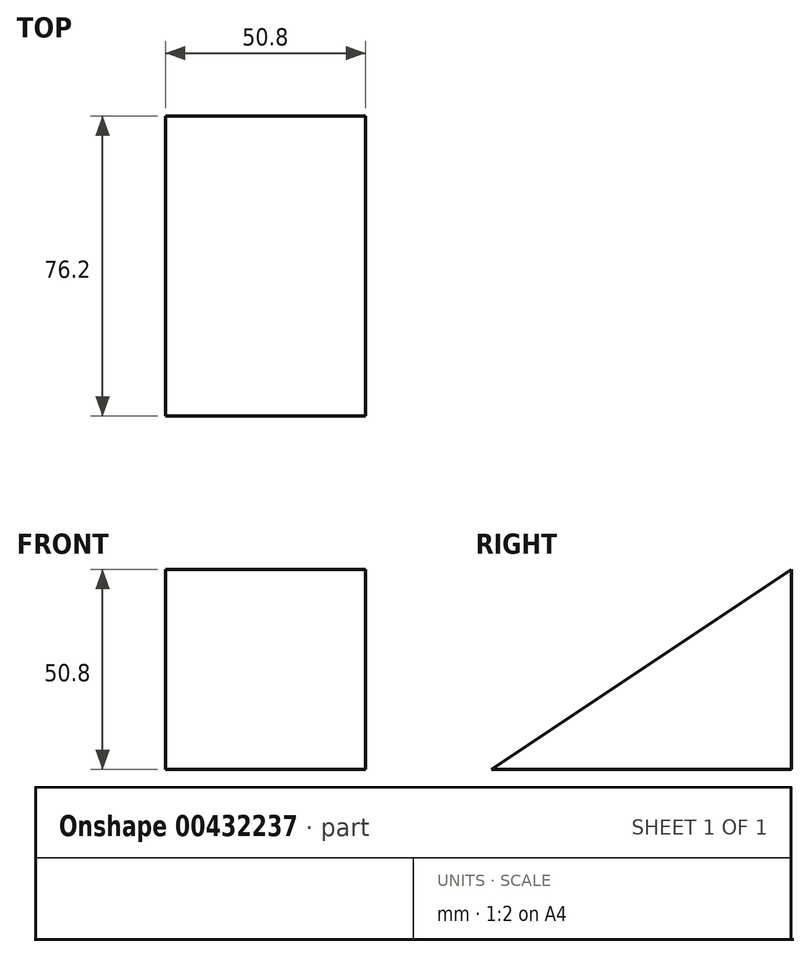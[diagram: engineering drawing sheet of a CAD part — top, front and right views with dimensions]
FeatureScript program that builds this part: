
annotation { "Feature Type Name" : "Feature", "Feature Type Description" : "" }
export const myFeature = defineFeature(function(context is Context, id is Id, definition is map)
    precondition{}
    {
        {
            var Q0;
            Q0=qCreatedBy(makeId("Right.planeOp"),FACE);
            var sketch = newSketch(context, id + "F0", { "sketchPlane" : qUnion([Q0])});
            skLineSegment(sketch, "E0", {"start": v(0, 0) * mm, "end": v(0, -50.8) * mm});
            skLineSegment(sketch, "E1", {"start": v(0, -50.8) * mm, "end": v(-76.2, -50.8) * mm});
            skLineSegment(sketch, "E2", {"start": v(-76.2, -50.8) * mm, "end": v(0, 0) * mm});
            skSolve(sketch);
        }
        {
            var Q0;
            Q0 = qSketchRegion(id + "F0", true);
            extrude(context, id + "F1", {"entities" : qUnion([Q0]), "depth" : 50.8 * mm});
        }
    });
